FCSTD DOCUMENT  (FreeCAD 0.19R0.19.2)
Label: v0_06
License: All rights reserved
LicenseURL: http://en.wikipedia.org/wiki/All_rights_reserved
objects: Sketcher::SketchObject×1
note: 1 computed .brp shape members not serialized (recipe doc carries the construction recipe); baked Part::Feature solids carry a one-line shape summary decoded from their .brp

FEATURE [Sketcher::SketchObject] Sketch
  FullyConstrained = true
  sketch-geometry (36):
    g0: LineSegment StartX=0 StartY=0 StartZ=0 EndX=111.35 EndY=0 EndZ=0
    g1: Circle CenterX=111.35 CenterY=-15.15 CenterZ=0 NormalX=0 NormalY=0 NormalZ=1 AngleXU=0 Radius=3.25
    g2: LineSegment StartX=111.35 StartY=0 StartZ=0 EndX=144.4 EndY=0 EndZ=0
    g3: LineSegment StartX=144.9 StartY=-7.5 StartZ=0 EndX=151.9 EndY=-7.5 EndZ=0
    g4: LineSegment StartX=111.35 StartY=0 StartZ=0 EndX=98.1 EndY=0 EndZ=0
    g5: Circle CenterX=81.35 CenterY=-6.2 CenterZ=0 NormalX=0 NormalY=0 NormalZ=1 AngleXU=0 Radius=1.3
    g6: Circle CenterX=61.25 CenterY=-6.2 CenterZ=0 NormalX=0 NormalY=0 NormalZ=1 AngleXU=0 Radius=1.3
    g7: LineSegment StartX=111.35 StartY=0 StartZ=0 EndX=81.35 EndY=0 EndZ=0
    g8: LineSegment StartX=144.4 StartY=0 StartZ=0 EndX=144.4 EndY=-7 EndZ=0
    g9: ArcOfCircle CenterX=144.9 CenterY=-7 CenterZ=0 NormalX=0 NormalY=0 NormalZ=1 AngleXU=0 Radius=0.5 StartAngle=3.14159 EndAngle=4.71239
    g10: Circle CenterX=81.35 CenterY=-14.2 CenterZ=0 NormalX=0 NormalY=0 NormalZ=1 AngleXU=0 Radius=1.3
    g11: Circle CenterX=61.25 CenterY=-14.2 CenterZ=0 NormalX=0 NormalY=0 NormalZ=1 AngleXU=0 Radius=1.3
    g12: LineSegment StartX=61.25 StartY=-15.5 StartZ=0 EndX=61.25 EndY=-20.4 EndZ=0
    g13: LineSegment StartX=61.25 StartY=-20.4 StartZ=0 EndX=104.85 EndY=-20.4 EndZ=0
    g14: LineSegment StartX=109.725 StartY=-21.65 StartZ=0 EndX=111.35 EndY=-21.65 EndZ=0
    g15-g19: Circle x5 (B-spline internal-alignment scaffolding for g20; pole/knot coordinates omitted)
    g20: BSplineCurve PolesCount=5 KnotsCount=3 Degree=3 IsPeriodic=0
    g21: GeomPoint X=104.85 Y=-20.4 Z=0
    g22: GeomPoint X=108.1 Y=-21.0125 Z=0
    g23: GeomPoint X=111.35 Y=-21.65 Z=0
    g24: LineSegment StartX=111.35 StartY=-21.65 StartZ=0 EndX=112.975 EndY=-21.65 EndZ=0
    g25-g29: Circle x5 (B-spline internal-alignment scaffolding for g30; pole/knot coordinates omitted)
    g30: BSplineCurve PolesCount=5 KnotsCount=3 Degree=3 IsPeriodic=0
    g31: GeomPoint X=111.35 Y=-21.65 Z=0
    g32: GeomPoint X=114.6 Y=-21.0125 Z=0
    g33: GeomPoint X=117.85 Y=-20.4 Z=0
    g34: LineSegment StartX=117.85 StartY=-20.4 StartZ=0 EndX=151.9 EndY=-20.4 EndZ=0
    g35: LineSegment StartX=151.9 StartY=-7.5 StartZ=0 EndX=151.9 EndY=-20.4 EndZ=0
  constraints (65):
    c: Coincident(g0,g-1)
    c: PointOnObject(g0,g-1)
    c: Distance(g0) = 111.35
    c: Radius(g1) = 3.25
    c: Block(g1)
    c: Horizontal(g2)
    c: Distance(g2) = 33.05
    c: Coincident(g2,g0)
    c: Horizontal(g4)
    c: Distance(g4) = 13.25
    c: Coincident(g4,g0)
    c: Horizontal(g7)
    c: Distance(g7) = 30
    c: Coincident(g7,g0)
    c: Block(g5)
    c: Block(g6)
    c: Vertical(g8)
    c: Distance(g8) = 7
    c: Coincident(g8,g2)
    c: Coincident(g9,g8)
    c: Coincident(g9,g3)
    c: Block(g3)
    c: Block(g9)
    c: Block(g10)
    c: Block(g11)
    c: Vertical(g12)
    c: Distance(g12) = 4.9
    c: Block(g12)
    c: Horizontal(g13)
    c: Coincident(g13,g12)
    c: Block(g13)
    c: Horizontal(g14)
    c: Distance(g14) = 1.625
    c: Coincident(g20,g13)
    c: Weight(g15) = 1
    c: Equal(g15,g16)
    c: Equal(g15,g17)
    c: Equal(g15,g18)
    c: Coincident(g18,g14)
    c: Equal(g15,g19)
    c: InternalAlignment(g15-g19 -> g20) x5
    c: InternalAlignment(g21,g20)
    c: InternalAlignment(g22,g20)
    c: InternalAlignment(g23,g20)
    c: Horizontal(g24)
    c: Distance(g24) = 1.625
    c: Weight(g25) = 1
    c: Equal(g25,g26)
    c: Coincident(g26,g24)
    c: Equal(g25,g27)
    c: Equal(g25,g28)
    c: Equal(g25,g29)
    c: InternalAlignment(g25-g29 -> g30) x5
    c: InternalAlignment(g31,g30)
    c: InternalAlignment(g32,g30)
    c: InternalAlignment(g33,g30)
    c: Block(g30)
    c: Block(g20)
    c: Horizontal(g34)
    c: Coincident(g34,g30)
    c: Vertical(g35)
    c: Coincident(g35,g3)
    c: Coincident(g35,g34)
    c: Block(g35)
    c: Block(g34)
